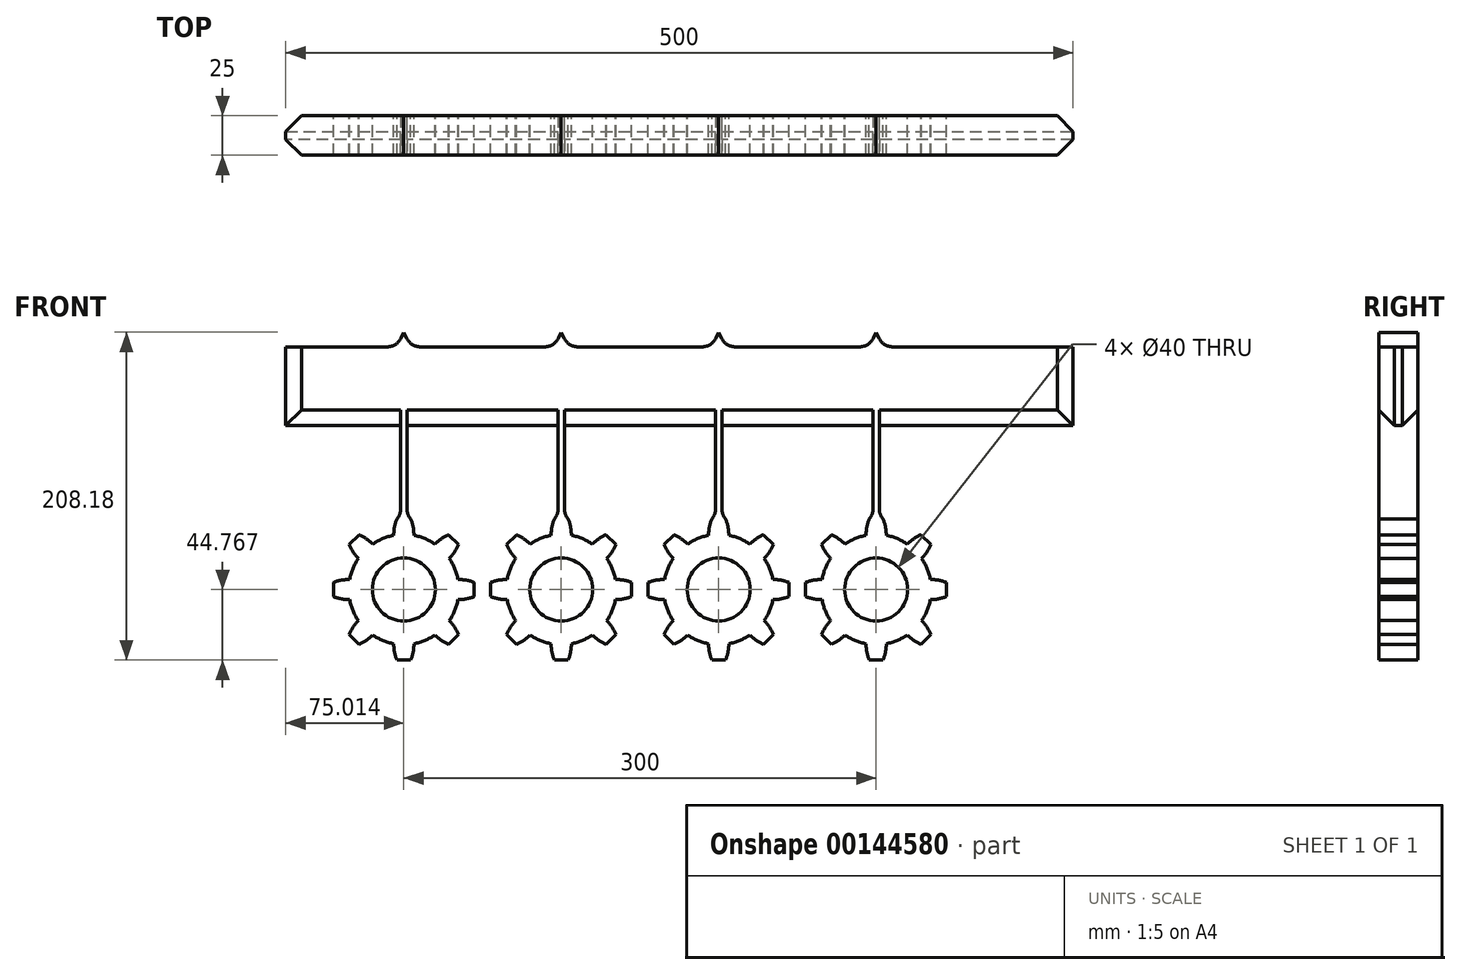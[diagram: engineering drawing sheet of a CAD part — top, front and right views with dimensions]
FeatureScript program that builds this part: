
annotation { "Feature Type Name" : "Feature", "Feature Type Description" : "" }
export const myFeature = defineFeature(function(context is Context, id is Id, definition is map)
    precondition{}
    {
        {
            var Q0;
            Q0=qCreatedBy(makeId("Front.planeOp"),FACE);
            var sketch = newSketch(context, id + "F0", { "sketchPlane" : qUnion([Q0])});
            skLineSegment(sketch, "E0.bottom", {"start": v(-250, 25) * mm, "end": v(-179.31, 25) * mm});
            skLineSegment(sketch, "E0.top", {"start": v(-250, -25) * mm, "end": v(-176.99, -25) * mm});
            skLineSegment(sketch, "E0.left", {"start": v(-250, 25) * mm, "end": v(-250, -25) * mm});
            skLineSegment(sketch, "E0.right", {"start": v(250, 25) * mm, "end": v(250, -25) * mm});
            skLineSegment(sketch, "E1", {"start": v(-174.99, 34.28) * mm, "end": v(-179.31, 25) * mm});
            skLineSegment(sketch, "E2", {"start": v(-174.99, 34.28) * mm, "end": v(-170.66, 25) * mm});
            skLineSegment(sketch, "E3.1.0.0", {"start": v(-74.99, 34.28) * mm, "end": v(-79.31, 25) * mm});
            skLineSegment(sketch, "E3.1.0.1", {"start": v(-74.99, 34.28) * mm, "end": v(-70.66, 25) * mm});
            skLineSegment(sketch, "E3.2.0.0", {"start": v(25.01, 34.28) * mm, "end": v(20.69, 25) * mm});
            skLineSegment(sketch, "E3.2.0.1", {"start": v(25.01, 34.28) * mm, "end": v(29.34, 25) * mm});
            skLineSegment(sketch, "E3.3.0.0", {"start": v(125.01, 34.28) * mm, "end": v(120.69, 25) * mm});
            skLineSegment(sketch, "E3.3.0.1", {"start": v(125.01, 34.28) * mm, "end": v(129.34, 25) * mm});
            skLineSegment(sketch, "E3.direction1", {"start": v(-170.66, 25) * mm, "end": v(-79.31, 25) * mm, "construction": true});
            skLineSegment(sketch, "E4.trimOffspring", {"start": v(-70.66, 25) * mm, "end": v(20.69, 25) * mm});
            skLineSegment(sketch, "E5.trimOffspring", {"start": v(-170.66, 25) * mm, "end": v(-79.31, 25) * mm});
            skLineSegment(sketch, "E6.trimOffspring", {"start": v(29.34, 25) * mm, "end": v(120.69, 25) * mm});
            skLineSegment(sketch, "E7.trimOffspring", {"start": v(129.34, 25) * mm, "end": v(250, 25) * mm});
            skCircle(sketch, "E8", {"center": v(-174.99, -129.13) * mm, "radius": 20 * mm});
            skArc(sketch, "E9", {"start": v(-179.41, -84.37) * mm, "mid": v(-180.9, -89.45) * mm, "end": v(-181.41, -94.73) * mm});
            skLineSegment(sketch, "E10", {"start": v(-179.41, -84.37) * mm, "end": v(-176.99, -84.37) * mm});
            skArc(sketch, "E11", {"start": v(-168.56, -94.73) * mm, "mid": v(-169.06, -89.45) * mm, "end": v(-170.56, -84.37) * mm});
            skArc(sketch, "E12.2.0", {"start": v(16.64, 197.56) * mm, "mid": v(12.99, 201.4) * mm, "end": v(8.67, 204.47) * mm});
            skLineSegment(sketch, "E12.2.1", {"start": v(16.64, 197.56) * mm, "end": v(12.21, 189.9) * mm});
            skArc(sketch, "E12.2.2", {"start": v(2.24, 193.34) * mm, "mid": v(7.06, 191.14) * mm, "end": v(12.21, 189.9) * mm});
            skPoint(sketch, "E12.center", {"position": v(0, 0) * mm});
            skArc(sketch, "E13.1.0", {"start": v(-209.77, -100.61) * mm, "mid": v(-207.23, -105.26) * mm, "end": v(-203.86, -109.35) * mm});
            skLineSegment(sketch, "E13.1.1", {"start": v(-209.77, -100.61) * mm, "end": v(-203.5, -94.35) * mm});
            skArc(sketch, "E13.1.2", {"start": v(-194.77, -100.26) * mm, "mid": v(-198.86, -96.89) * mm, "end": v(-203.5, -94.35) * mm});
            skArc(sketch, "E13.2.0", {"start": v(-219.75, -133.56) * mm, "mid": v(-214.67, -135.05) * mm, "end": v(-209.4, -135.56) * mm});
            skLineSegment(sketch, "E13.2.1", {"start": v(-219.75, -133.56) * mm, "end": v(-219.75, -124.7) * mm});
            skArc(sketch, "E13.2.2", {"start": v(-209.4, -122.7) * mm, "mid": v(-214.67, -123.21) * mm, "end": v(-219.75, -124.7) * mm});
            skArc(sketch, "E13.3.0", {"start": v(-203.5, -163.92) * mm, "mid": v(-198.86, -161.38) * mm, "end": v(-194.77, -158) * mm});
            skLineSegment(sketch, "E13.3.1", {"start": v(-203.5, -163.92) * mm, "end": v(-209.77, -157.66) * mm});
            skArc(sketch, "E13.3.2", {"start": v(-203.86, -148.92) * mm, "mid": v(-207.23, -153) * mm, "end": v(-209.77, -157.66) * mm});
            skArc(sketch, "E13.4.0", {"start": v(-170.56, -173.9) * mm, "mid": v(-169.06, -168.81) * mm, "end": v(-168.56, -163.54) * mm});
            skLineSegment(sketch, "E13.4.1", {"start": v(-170.56, -173.9) * mm, "end": v(-179.41, -173.9) * mm});
            skArc(sketch, "E13.4.2", {"start": v(-181.41, -163.54) * mm, "mid": v(-180.9, -168.81) * mm, "end": v(-179.41, -173.9) * mm});
            skArc(sketch, "E13.5.0", {"start": v(-140.2, -157.66) * mm, "mid": v(-142.74, -153) * mm, "end": v(-146.11, -148.92) * mm});
            skLineSegment(sketch, "E13.5.1", {"start": v(-140.2, -157.66) * mm, "end": v(-146.46, -163.92) * mm});
            skArc(sketch, "E13.5.2", {"start": v(-155.2, -158) * mm, "mid": v(-151.12, -161.38) * mm, "end": v(-146.46, -163.92) * mm});
            skArc(sketch, "E13.6.0", {"start": v(-130.22, -124.7) * mm, "mid": v(-135.3, -123.21) * mm, "end": v(-140.58, -122.7) * mm});
            skLineSegment(sketch, "E13.6.1", {"start": v(-130.22, -124.7) * mm, "end": v(-130.22, -133.56) * mm});
            skArc(sketch, "E13.6.2", {"start": v(-140.58, -135.56) * mm, "mid": v(-135.3, -135.05) * mm, "end": v(-130.22, -133.56) * mm});
            skArc(sketch, "E13.7.0", {"start": v(-146.46, -94.35) * mm, "mid": v(-151.12, -96.89) * mm, "end": v(-155.2, -100.26) * mm});
            skLineSegment(sketch, "E13.7.1", {"start": v(-146.46, -94.35) * mm, "end": v(-140.2, -100.61) * mm});
            skArc(sketch, "E13.7.2", {"start": v(-146.11, -109.35) * mm, "mid": v(-142.74, -105.26) * mm, "end": v(-140.2, -100.61) * mm});
            skArc(sketch, "E14.trimOffspring", {"start": v(-203.86, -109.35) * mm, "mid": v(-207.32, -115.74) * mm, "end": v(-209.4, -122.7) * mm});
            skArc(sketch, "E15.trimOffspring", {"start": v(-194.77, -158) * mm, "mid": v(-188.38, -161.47) * mm, "end": v(-181.41, -163.54) * mm});
            skArc(sketch, "E16.trimOffspring", {"start": v(-168.56, -163.54) * mm, "mid": v(-161.6, -161.47) * mm, "end": v(-155.2, -158) * mm});
            skArc(sketch, "E17.trimOffspring", {"start": v(-209.4, -135.56) * mm, "mid": v(-207.32, -142.53) * mm, "end": v(-203.86, -148.92) * mm});
            skArc(sketch, "E18.trimOffspring", {"start": v(-155.2, -100.26) * mm, "mid": v(-161.6, -96.8) * mm, "end": v(-168.56, -94.73) * mm});
            skArc(sketch, "E19.trimOffspring", {"start": v(-140.58, -122.7) * mm, "mid": v(-142.65, -115.74) * mm, "end": v(-146.11, -109.35) * mm});
            skArc(sketch, "E20.trimOffspring", {"start": v(-146.11, -148.92) * mm, "mid": v(-142.65, -142.53) * mm, "end": v(-140.58, -135.56) * mm});
            skLineSegment(sketch, "E21", {"start": v(-174.99, -84.37) * mm, "end": v(-174.99, -25) * mm, "construction": true});
            skLineSegment(sketch, "E22", {"start": v(-176.99, -84.37) * mm, "end": v(-176.99, -25) * mm});
            skLineSegment(sketch, "E23", {"start": v(-172.99, -84.37) * mm, "end": v(-172.99, -25) * mm});
            skLineSegment(sketch, "E24.trimOffspring", {"start": v(-172.99, -25) * mm, "end": v(23.01, -25) * mm});
            skLineSegment(sketch, "E25.trimOffspring", {"start": v(-172.99, -84.37) * mm, "end": v(-170.56, -84.37) * mm});
            skArc(sketch, "E26", {"start": v(-181.41, -94.73) * mm, "mid": v(-188.38, -96.8) * mm, "end": v(-194.77, -100.26) * mm});
            skCircle(sketch, "E27.1.0.0", {"center": v(-74.99, -129.13) * mm, "radius": 20 * mm});
            skPoint(sketch, "E27.1.0.1", {"position": v(-74.99, -129.13) * mm});
            skArc(sketch, "E27.1.0.2", {"start": v(-94.77, -100.26) * mm, "mid": v(-98.86, -96.89) * mm, "end": v(-103.5, -94.35) * mm});
            skArc(sketch, "E27.1.0.3", {"start": v(-94.77, -158) * mm, "mid": v(-88.38, -161.47) * mm, "end": v(-81.41, -163.54) * mm});
            skArc(sketch, "E27.1.0.4", {"start": v(-109.4, -122.7) * mm, "mid": v(-114.67, -123.21) * mm, "end": v(-119.75, -124.7) * mm});
            skArc(sketch, "E27.1.0.5", {"start": v(-70.56, -173.9) * mm, "mid": v(-69.06, -168.81) * mm, "end": v(-68.56, -163.54) * mm});
            skArc(sketch, "E27.1.0.6", {"start": v(-55.2, -100.26) * mm, "mid": v(-61.6, -96.8) * mm, "end": v(-68.56, -94.73) * mm});
            skArc(sketch, "E27.1.0.7", {"start": v(-40.2, -157.66) * mm, "mid": v(-42.74, -153) * mm, "end": v(-46.11, -148.92) * mm});
            skArc(sketch, "E27.1.0.8", {"start": v(-40.58, -122.7) * mm, "mid": v(-42.65, -115.74) * mm, "end": v(-46.11, -109.35) * mm});
            skArc(sketch, "E27.1.0.9", {"start": v(-46.46, -94.35) * mm, "mid": v(-51.12, -96.89) * mm, "end": v(-55.2, -100.26) * mm});
            skArc(sketch, "E27.1.0.10", {"start": v(-119.75, -133.56) * mm, "mid": v(-114.67, -135.05) * mm, "end": v(-109.4, -135.56) * mm});
            skLineSegment(sketch, "E27.1.0.11", {"start": v(-70.56, -173.9) * mm, "end": v(-79.41, -173.9) * mm});
            skArc(sketch, "E27.1.0.12", {"start": v(-68.56, -94.73) * mm, "mid": v(-69.06, -89.45) * mm, "end": v(-70.56, -84.37) * mm});
            skArc(sketch, "E27.1.0.13", {"start": v(-55.2, -158) * mm, "mid": v(-51.12, -161.38) * mm, "end": v(-46.46, -163.92) * mm});
            skLineSegment(sketch, "E27.1.0.14", {"start": v(-46.46, -94.35) * mm, "end": v(-40.2, -100.61) * mm});
            skArc(sketch, "E27.1.0.15", {"start": v(-40.58, -135.56) * mm, "mid": v(-35.3, -135.05) * mm, "end": v(-30.22, -133.56) * mm});
            skLineSegment(sketch, "E27.1.0.16", {"start": v(-109.77, -100.61) * mm, "end": v(-103.5, -94.35) * mm});
            skArc(sketch, "E27.1.0.17", {"start": v(-81.41, -94.73) * mm, "mid": v(-88.38, -96.8) * mm, "end": v(-94.77, -100.26) * mm});
            skLineSegment(sketch, "E27.1.0.18", {"start": v(-30.22, -124.7) * mm, "end": v(-30.22, -133.56) * mm});
            skArc(sketch, "E27.1.0.19", {"start": v(-103.86, -109.35) * mm, "mid": v(-107.32, -115.74) * mm, "end": v(-109.4, -122.7) * mm});
            skArc(sketch, "E27.1.0.20", {"start": v(-68.56, -163.54) * mm, "mid": v(-61.6, -161.47) * mm, "end": v(-55.2, -158) * mm});
            skArc(sketch, "E27.1.0.21", {"start": v(-109.77, -100.61) * mm, "mid": v(-107.23, -105.26) * mm, "end": v(-103.86, -109.35) * mm});
            skArc(sketch, "E27.1.0.22", {"start": v(-81.41, -163.54) * mm, "mid": v(-80.9, -168.81) * mm, "end": v(-79.41, -173.9) * mm});
            skArc(sketch, "E27.1.0.23", {"start": v(-79.41, -84.37) * mm, "mid": v(-80.9, -89.45) * mm, "end": v(-81.41, -94.73) * mm});
            skArc(sketch, "E27.1.0.24", {"start": v(-46.11, -148.92) * mm, "mid": v(-42.65, -142.53) * mm, "end": v(-40.58, -135.56) * mm});
            skLineSegment(sketch, "E27.1.0.25", {"start": v(-40.2, -157.66) * mm, "end": v(-46.46, -163.92) * mm});
            skLineSegment(sketch, "E27.1.0.26", {"start": v(-119.75, -133.56) * mm, "end": v(-119.75, -124.7) * mm});
            skArc(sketch, "E27.1.0.27", {"start": v(-46.11, -109.35) * mm, "mid": v(-42.74, -105.26) * mm, "end": v(-40.2, -100.61) * mm});
            skArc(sketch, "E27.1.0.28", {"start": v(-103.86, -148.92) * mm, "mid": v(-107.23, -153) * mm, "end": v(-109.77, -157.66) * mm});
            skArc(sketch, "E27.1.0.29", {"start": v(-109.4, -135.56) * mm, "mid": v(-107.32, -142.53) * mm, "end": v(-103.86, -148.92) * mm});
            skArc(sketch, "E27.1.0.30", {"start": v(-103.5, -163.92) * mm, "mid": v(-98.86, -161.38) * mm, "end": v(-94.77, -158) * mm});
            skArc(sketch, "E27.1.0.31", {"start": v(-30.22, -124.7) * mm, "mid": v(-35.3, -123.21) * mm, "end": v(-40.58, -122.7) * mm});
            skLineSegment(sketch, "E27.1.0.32", {"start": v(-103.5, -163.92) * mm, "end": v(-109.77, -157.66) * mm});
            skLineSegment(sketch, "E27.1.0.33", {"start": v(-79.41, -84.37) * mm, "end": v(-76.99, -84.37) * mm});
            skLineSegment(sketch, "E27.1.0.34", {"start": v(-72.99, -84.37) * mm, "end": v(-70.56, -84.37) * mm});
            skLineSegment(sketch, "E27.1.0.35", {"start": v(-76.99, -84.37) * mm, "end": v(-76.99, -25) * mm});
            skLineSegment(sketch, "E27.1.0.36", {"start": v(-72.99, -84.37) * mm, "end": v(-72.99, -25) * mm});
            skCircle(sketch, "E27.2.0.0", {"center": v(25.01, -129.13) * mm, "radius": 20 * mm});
            skPoint(sketch, "E27.2.0.1", {"position": v(25.01, -129.13) * mm});
            skArc(sketch, "E27.2.0.2", {"start": v(5.23, -100.26) * mm, "mid": v(1.14, -96.89) * mm, "end": v(-3.5, -94.35) * mm});
            skArc(sketch, "E27.2.0.3", {"start": v(5.23, -158) * mm, "mid": v(11.62, -161.47) * mm, "end": v(18.59, -163.54) * mm});
            skArc(sketch, "E27.2.0.4", {"start": v(-9.4, -122.7) * mm, "mid": v(-14.67, -123.21) * mm, "end": v(-19.75, -124.7) * mm});
            skArc(sketch, "E27.2.0.5", {"start": v(29.44, -173.9) * mm, "mid": v(30.94, -168.81) * mm, "end": v(31.44, -163.54) * mm});
            skArc(sketch, "E27.2.0.6", {"start": v(44.8, -100.26) * mm, "mid": v(38.4, -96.8) * mm, "end": v(31.44, -94.73) * mm});
            skArc(sketch, "E27.2.0.7", {"start": v(59.8, -157.66) * mm, "mid": v(57.26, -153) * mm, "end": v(53.89, -148.92) * mm});
            skArc(sketch, "E27.2.0.8", {"start": v(59.42, -122.7) * mm, "mid": v(57.35, -115.74) * mm, "end": v(53.89, -109.35) * mm});
            skArc(sketch, "E27.2.0.9", {"start": v(53.54, -94.35) * mm, "mid": v(48.88, -96.89) * mm, "end": v(44.8, -100.26) * mm});
            skArc(sketch, "E27.2.0.10", {"start": v(-19.75, -133.56) * mm, "mid": v(-14.67, -135.05) * mm, "end": v(-9.4, -135.56) * mm});
            skLineSegment(sketch, "E27.2.0.11", {"start": v(29.44, -173.9) * mm, "end": v(20.59, -173.9) * mm});
            skArc(sketch, "E27.2.0.12", {"start": v(31.44, -94.73) * mm, "mid": v(30.94, -89.45) * mm, "end": v(29.44, -84.37) * mm});
            skArc(sketch, "E27.2.0.13", {"start": v(44.8, -158) * mm, "mid": v(48.88, -161.38) * mm, "end": v(53.54, -163.92) * mm});
            skLineSegment(sketch, "E27.2.0.14", {"start": v(53.54, -94.35) * mm, "end": v(59.8, -100.61) * mm});
            skArc(sketch, "E27.2.0.15", {"start": v(59.42, -135.56) * mm, "mid": v(64.7, -135.05) * mm, "end": v(69.78, -133.56) * mm});
            skLineSegment(sketch, "E27.2.0.16", {"start": v(-9.77, -100.61) * mm, "end": v(-3.5, -94.35) * mm});
            skArc(sketch, "E27.2.0.17", {"start": v(18.59, -94.73) * mm, "mid": v(11.62, -96.8) * mm, "end": v(5.23, -100.26) * mm});
            skLineSegment(sketch, "E27.2.0.18", {"start": v(69.78, -124.7) * mm, "end": v(69.78, -133.56) * mm});
            skArc(sketch, "E27.2.0.19", {"start": v(-3.86, -109.35) * mm, "mid": v(-7.32, -115.74) * mm, "end": v(-9.4, -122.7) * mm});
            skArc(sketch, "E27.2.0.20", {"start": v(31.44, -163.54) * mm, "mid": v(38.4, -161.47) * mm, "end": v(44.8, -158) * mm});
            skArc(sketch, "E27.2.0.21", {"start": v(-9.77, -100.61) * mm, "mid": v(-7.23, -105.26) * mm, "end": v(-3.86, -109.35) * mm});
            skArc(sketch, "E27.2.0.22", {"start": v(18.59, -163.54) * mm, "mid": v(19.1, -168.81) * mm, "end": v(20.59, -173.9) * mm});
            skArc(sketch, "E27.2.0.23", {"start": v(20.59, -84.37) * mm, "mid": v(19.1, -89.45) * mm, "end": v(18.59, -94.73) * mm});
            skArc(sketch, "E27.2.0.24", {"start": v(53.89, -148.92) * mm, "mid": v(57.35, -142.53) * mm, "end": v(59.42, -135.56) * mm});
            skLineSegment(sketch, "E27.2.0.25", {"start": v(59.8, -157.66) * mm, "end": v(53.54, -163.92) * mm});
            skLineSegment(sketch, "E27.2.0.26", {"start": v(-19.75, -133.56) * mm, "end": v(-19.75, -124.7) * mm});
            skArc(sketch, "E27.2.0.27", {"start": v(53.89, -109.35) * mm, "mid": v(57.26, -105.26) * mm, "end": v(59.8, -100.61) * mm});
            skArc(sketch, "E27.2.0.28", {"start": v(-3.86, -148.92) * mm, "mid": v(-7.23, -153) * mm, "end": v(-9.77, -157.66) * mm});
            skArc(sketch, "E27.2.0.29", {"start": v(-9.4, -135.56) * mm, "mid": v(-7.32, -142.53) * mm, "end": v(-3.86, -148.92) * mm});
            skArc(sketch, "E27.2.0.30", {"start": v(-3.5, -163.92) * mm, "mid": v(1.14, -161.38) * mm, "end": v(5.23, -158) * mm});
            skArc(sketch, "E27.2.0.31", {"start": v(69.78, -124.7) * mm, "mid": v(64.7, -123.21) * mm, "end": v(59.42, -122.7) * mm});
            skLineSegment(sketch, "E27.2.0.32", {"start": v(-3.5, -163.92) * mm, "end": v(-9.77, -157.66) * mm});
            skLineSegment(sketch, "E27.2.0.33", {"start": v(20.59, -84.37) * mm, "end": v(23.01, -84.37) * mm});
            skLineSegment(sketch, "E27.2.0.34", {"start": v(27.01, -84.37) * mm, "end": v(29.44, -84.37) * mm});
            skLineSegment(sketch, "E27.2.0.35", {"start": v(23.01, -84.37) * mm, "end": v(23.01, -25) * mm});
            skLineSegment(sketch, "E27.2.0.36", {"start": v(27.01, -84.37) * mm, "end": v(27.01, -25) * mm});
            skCircle(sketch, "E27.3.0.0", {"center": v(125.01, -129.13) * mm, "radius": 20 * mm});
            skPoint(sketch, "E27.3.0.1", {"position": v(125.01, -129.13) * mm});
            skArc(sketch, "E27.3.0.2", {"start": v(105.23, -100.26) * mm, "mid": v(101.14, -96.89) * mm, "end": v(96.5, -94.35) * mm});
            skArc(sketch, "E27.3.0.3", {"start": v(105.23, -158) * mm, "mid": v(111.62, -161.47) * mm, "end": v(118.59, -163.54) * mm});
            skArc(sketch, "E27.3.0.4", {"start": v(90.6, -122.7) * mm, "mid": v(85.33, -123.21) * mm, "end": v(80.25, -124.7) * mm});
            skArc(sketch, "E27.3.0.5", {"start": v(129.44, -173.9) * mm, "mid": v(130.94, -168.81) * mm, "end": v(131.44, -163.54) * mm});
            skArc(sketch, "E27.3.0.6", {"start": v(144.8, -100.26) * mm, "mid": v(138.4, -96.8) * mm, "end": v(131.44, -94.73) * mm});
            skArc(sketch, "E27.3.0.7", {"start": v(159.8, -157.66) * mm, "mid": v(157.26, -153) * mm, "end": v(153.89, -148.92) * mm});
            skArc(sketch, "E27.3.0.8", {"start": v(159.42, -122.7) * mm, "mid": v(157.35, -115.74) * mm, "end": v(153.89, -109.35) * mm});
            skArc(sketch, "E27.3.0.9", {"start": v(153.54, -94.35) * mm, "mid": v(148.88, -96.89) * mm, "end": v(144.8, -100.26) * mm});
            skArc(sketch, "E27.3.0.10", {"start": v(80.25, -133.56) * mm, "mid": v(85.33, -135.05) * mm, "end": v(90.6, -135.56) * mm});
            skLineSegment(sketch, "E27.3.0.11", {"start": v(129.44, -173.9) * mm, "end": v(120.59, -173.9) * mm});
            skArc(sketch, "E27.3.0.12", {"start": v(131.44, -94.73) * mm, "mid": v(130.94, -89.45) * mm, "end": v(129.44, -84.37) * mm});
            skArc(sketch, "E27.3.0.13", {"start": v(144.8, -158) * mm, "mid": v(148.88, -161.38) * mm, "end": v(153.54, -163.92) * mm});
            skLineSegment(sketch, "E27.3.0.14", {"start": v(153.54, -94.35) * mm, "end": v(159.8, -100.61) * mm});
            skArc(sketch, "E27.3.0.15", {"start": v(159.42, -135.56) * mm, "mid": v(164.7, -135.05) * mm, "end": v(169.78, -133.56) * mm});
            skLineSegment(sketch, "E27.3.0.16", {"start": v(90.23, -100.61) * mm, "end": v(96.5, -94.35) * mm});
            skArc(sketch, "E27.3.0.17", {"start": v(118.59, -94.73) * mm, "mid": v(111.62, -96.8) * mm, "end": v(105.23, -100.26) * mm});
            skLineSegment(sketch, "E27.3.0.18", {"start": v(169.78, -124.7) * mm, "end": v(169.78, -133.56) * mm});
            skArc(sketch, "E27.3.0.19", {"start": v(96.14, -109.35) * mm, "mid": v(92.68, -115.74) * mm, "end": v(90.6, -122.7) * mm});
            skArc(sketch, "E27.3.0.20", {"start": v(131.44, -163.54) * mm, "mid": v(138.4, -161.47) * mm, "end": v(144.8, -158) * mm});
            skArc(sketch, "E27.3.0.21", {"start": v(90.23, -100.61) * mm, "mid": v(92.77, -105.26) * mm, "end": v(96.14, -109.35) * mm});
            skArc(sketch, "E27.3.0.22", {"start": v(118.59, -163.54) * mm, "mid": v(119.1, -168.81) * mm, "end": v(120.59, -173.9) * mm});
            skArc(sketch, "E27.3.0.23", {"start": v(120.59, -84.37) * mm, "mid": v(119.1, -89.45) * mm, "end": v(118.59, -94.73) * mm});
            skArc(sketch, "E27.3.0.24", {"start": v(153.89, -148.92) * mm, "mid": v(157.35, -142.53) * mm, "end": v(159.42, -135.56) * mm});
            skLineSegment(sketch, "E27.3.0.25", {"start": v(159.8, -157.66) * mm, "end": v(153.54, -163.92) * mm});
            skLineSegment(sketch, "E27.3.0.26", {"start": v(80.25, -133.56) * mm, "end": v(80.25, -124.7) * mm});
            skArc(sketch, "E27.3.0.27", {"start": v(153.89, -109.35) * mm, "mid": v(157.26, -105.26) * mm, "end": v(159.8, -100.61) * mm});
            skArc(sketch, "E27.3.0.28", {"start": v(96.14, -148.92) * mm, "mid": v(92.77, -153) * mm, "end": v(90.23, -157.66) * mm});
            skArc(sketch, "E27.3.0.29", {"start": v(90.6, -135.56) * mm, "mid": v(92.68, -142.53) * mm, "end": v(96.14, -148.92) * mm});
            skArc(sketch, "E27.3.0.30", {"start": v(96.5, -163.92) * mm, "mid": v(101.14, -161.38) * mm, "end": v(105.23, -158) * mm});
            skArc(sketch, "E27.3.0.31", {"start": v(169.78, -124.7) * mm, "mid": v(164.7, -123.21) * mm, "end": v(159.42, -122.7) * mm});
            skLineSegment(sketch, "E27.3.0.32", {"start": v(96.5, -163.92) * mm, "end": v(90.23, -157.66) * mm});
            skLineSegment(sketch, "E27.3.0.33", {"start": v(120.59, -84.37) * mm, "end": v(123.01, -84.37) * mm});
            skLineSegment(sketch, "E27.3.0.34", {"start": v(127.01, -84.37) * mm, "end": v(129.44, -84.37) * mm});
            skLineSegment(sketch, "E27.3.0.35", {"start": v(123.01, -84.37) * mm, "end": v(123.01, -25) * mm});
            skLineSegment(sketch, "E27.3.0.36", {"start": v(127.01, -84.37) * mm, "end": v(127.01, -25) * mm});
            skLineSegment(sketch, "E27.direction1", {"start": v(-203.5, -163.92) * mm, "end": v(-103.5, -163.92) * mm, "construction": true});
            skLineSegment(sketch, "E28.trimOffspring", {"start": v(127.01, -25) * mm, "end": v(250, -25) * mm});
            skLineSegment(sketch, "E29.trimOffspring", {"start": v(27.01, -25) * mm, "end": v(123.01, -25) * mm});
            skSolve(sketch);
        }
        {
            var Q0;
            Q0 = qSketchRegion(id + "F0", true);
            extrude(context, id + "F1", {"entities" : qUnion([Q0]), "endBound" : BoundingType.SYMMETRIC, "depth" : 25 * mm});
        }
        {
            var Q0;
            Q0=makeQuery(id+"F1.opExtrude","SWEPT_EDGE",EDGE,{"disambiguationData":[OSD([sQuery(id+"F0.wireOp",EDGE,"E0.bottom"),sQuery(id+"F0.wireOp",EDGE,"E1")])]});
            var Q1;
            Q1=makeQuery(id+"F1.opExtrude","SWEPT_EDGE",EDGE,{"disambiguationData":[OSD([sQuery(id+"F0.wireOp",EDGE,"E10"),sQuery(id+"F0.wireOp",EDGE,"E22")])]});
            var Q2;
            Q2=makeQuery(id+"F1.opExtrude","SWEPT_EDGE",EDGE,{"disambiguationData":[OSD([sQuery(id+"F0.wireOp",EDGE,"E3.1.0.0"),sQuery(id+"F0.wireOp",EDGE,"E5.trimOffspring")])]});
            var Q3;
            Q3=makeQuery(id+"F1.opExtrude","SWEPT_EDGE",EDGE,{"disambiguationData":[OSD([sQuery(id+"F0.wireOp",EDGE,"E3.2.0.0"),sQuery(id+"F0.wireOp",EDGE,"E4.trimOffspring")])]});
            var Q4;
            Q4=makeQuery(id+"F1.opExtrude","SWEPT_EDGE",EDGE,{"disambiguationData":[OSD([sQuery(id+"F0.wireOp",EDGE,"E3.3.0.0"),sQuery(id+"F0.wireOp",EDGE,"E6.trimOffspring")])]});
            var Q5;
            Q5=makeQuery(id+"F1.opExtrude","SWEPT_EDGE",EDGE,{"disambiguationData":[OSD([sQuery(id+"F0.wireOp",EDGE,"E27.3.0.33"),sQuery(id+"F0.wireOp",EDGE,"E27.3.0.35")])]});
            var Q6;
            Q6=makeQuery(id+"F1.opExtrude","SWEPT_EDGE",EDGE,{"disambiguationData":[OSD([sQuery(id+"F0.wireOp",EDGE,"E27.2.0.33"),sQuery(id+"F0.wireOp",EDGE,"E27.2.0.35")])]});
            var Q7;
            Q7=makeQuery(id+"F1.opExtrude","SWEPT_EDGE",EDGE,{"disambiguationData":[OSD([sQuery(id+"F0.wireOp",EDGE,"E27.1.0.33"),sQuery(id+"F0.wireOp",EDGE,"E27.1.0.35")])]});
            var Q8;
            Q8=makeQuery(id+"F1.opExtrude","SWEPT_EDGE",EDGE,{"disambiguationData":[OSD([sQuery(id+"F0.wireOp",EDGE,"E2"),sQuery(id+"F0.wireOp",EDGE,"E5.trimOffspring")])]});
            var Q9;
            Q9=makeQuery(id+"F1.opExtrude","SWEPT_EDGE",EDGE,{"disambiguationData":[OSD([sQuery(id+"F0.wireOp",EDGE,"E3.1.0.1"),sQuery(id+"F0.wireOp",EDGE,"E4.trimOffspring")])]});
            var Q10;
            Q10=makeQuery(id+"F1.opExtrude","SWEPT_EDGE",EDGE,{"disambiguationData":[OSD([sQuery(id+"F0.wireOp",EDGE,"E3.2.0.1"),sQuery(id+"F0.wireOp",EDGE,"E6.trimOffspring")])]});
            var Q11;
            Q11=makeQuery(id+"F1.opExtrude","SWEPT_EDGE",EDGE,{"disambiguationData":[OSD([sQuery(id+"F0.wireOp",EDGE,"E3.3.0.1"),sQuery(id+"F0.wireOp",EDGE,"E7.trimOffspring")])]});
            var Q12;
            Q12=makeQuery(id+"F1.opExtrude","SWEPT_EDGE",EDGE,{"disambiguationData":[OSD([sQuery(id+"F0.wireOp",EDGE,"E27.1.0.34"),sQuery(id+"F0.wireOp",EDGE,"E27.1.0.36")])]});
            var Q13;
            Q13=makeQuery(id+"F1.opExtrude","SWEPT_EDGE",EDGE,{"disambiguationData":[OSD([sQuery(id+"F0.wireOp",EDGE,"E23"),sQuery(id+"F0.wireOp",EDGE,"E25.trimOffspring")])]});
            var Q14;
            Q14=makeQuery(id+"F1.opExtrude","SWEPT_EDGE",EDGE,{"disambiguationData":[OSD([sQuery(id+"F0.wireOp",EDGE,"E27.2.0.34"),sQuery(id+"F0.wireOp",EDGE,"E27.2.0.36")])]});
            var Q15;
            Q15=makeQuery(id+"F1.opExtrude","SWEPT_EDGE",EDGE,{"disambiguationData":[OSD([sQuery(id+"F0.wireOp",EDGE,"E27.3.0.34"),sQuery(id+"F0.wireOp",EDGE,"E27.3.0.36")])]});
            fillet(context, id + "F2", {"entities" : qUnion([Q0, Q1, Q2, Q3, Q4, Q5, Q6, Q7, Q8, Q9, Q10, Q11, Q12, Q13, Q14, Q15]), "radius" : 10 * mm, "tangentPropagation" : true, "allowEdgeOverflow" : false});
        }
        {
            var Q0;
            Q0=makeQuery(id+"F1.opExtrude","CAP_EDGE",EDGE,{"disambiguationData":[OSD([sQuery(id+"F0.wireOp",EDGE,"E0.left")])],"isStart":false});
            var Q1;
            Q1=makeQuery(id+"F1.opExtrude","CAP_EDGE",EDGE,{"disambiguationData":[OSD([sQuery(id+"F0.wireOp",EDGE,"E0.top")])],"isStart":false});
            var Q2;
            {var subQ0=sQuery(id+"F0.wireOp",EDGE,"E24.trimOffspring");Q2=makeQuery(id+"F1.opExtrude","CAP_EDGE",EDGE,{"disambiguationData":[OSD([subQ0]),TDD([makeQuery(id+"F0.imprint","IMPRINT",EDGE,{"disambiguationData":[TD([[makeQuery(id+"F0.imprint","INTERSECT",VERTEX,{"derivedFrom":[sQuery(id+"F0.wireOp",EDGE,"E23"),subQ0]}),-1.0]])],"derivedFrom":subQ0})])],"isStart":false});}
            var Q3;
            {var subQ0=sQuery(id+"F0.wireOp",EDGE,"E24.trimOffspring");Q3=makeQuery(id+"F1.opExtrude","CAP_EDGE",EDGE,{"disambiguationData":[OSD([subQ0]),TDD([makeQuery(id+"F0.imprint","IMPRINT",EDGE,{"disambiguationData":[TD([[makeQuery(id+"F0.imprint","INTERSECT",VERTEX,{"derivedFrom":[subQ0,sQuery(id+"F0.wireOp",EDGE,"E27.2.0.35")]}),1.0]])],"derivedFrom":subQ0})])],"isStart":false});}
            var Q4;
            Q4=makeQuery(id+"F1.opExtrude","CAP_EDGE",EDGE,{"disambiguationData":[OSD([sQuery(id+"F0.wireOp",EDGE,"E29.trimOffspring")])],"isStart":false});
            var Q5;
            Q5=makeQuery(id+"F1.opExtrude","CAP_EDGE",EDGE,{"disambiguationData":[OSD([sQuery(id+"F0.wireOp",EDGE,"E28.trimOffspring")])],"isStart":false});
            var Q6;
            Q6=makeQuery(id+"F1.opExtrude","CAP_EDGE",EDGE,{"disambiguationData":[OSD([sQuery(id+"F0.wireOp",EDGE,"E0.right")])],"isStart":true});
            var Q7;
            Q7=makeQuery(id+"F1.opExtrude","CAP_EDGE",EDGE,{"disambiguationData":[OSD([sQuery(id+"F0.wireOp",EDGE,"E0.left")])],"isStart":true});
            var Q8;
            Q8=makeQuery(id+"F1.opExtrude","CAP_EDGE",EDGE,{"disambiguationData":[OSD([sQuery(id+"F0.wireOp",EDGE,"E0.top")])],"isStart":true});
            var Q9;
            {var subQ0=sQuery(id+"F0.wireOp",EDGE,"E24.trimOffspring");Q9=makeQuery(id+"F1.opExtrude","CAP_EDGE",EDGE,{"disambiguationData":[OSD([subQ0]),TDD([makeQuery(id+"F0.imprint","IMPRINT",EDGE,{"disambiguationData":[TD([[makeQuery(id+"F0.imprint","INTERSECT",VERTEX,{"derivedFrom":[sQuery(id+"F0.wireOp",EDGE,"E23"),subQ0]}),-1.0]])],"derivedFrom":subQ0})])],"isStart":true});}
            var Q10;
            Q10=makeQuery(id+"F1.opExtrude","CAP_EDGE",EDGE,{"disambiguationData":[OSD([sQuery(id+"F0.wireOp",EDGE,"E28.trimOffspring")])],"isStart":true});
            var Q11;
            Q11=makeQuery(id+"F1.opExtrude","CAP_EDGE",EDGE,{"disambiguationData":[OSD([sQuery(id+"F0.wireOp",EDGE,"E29.trimOffspring")])],"isStart":true});
            var Q12;
            {var subQ0=sQuery(id+"F0.wireOp",EDGE,"E24.trimOffspring");Q12=makeQuery(id+"F1.opExtrude","CAP_EDGE",EDGE,{"disambiguationData":[OSD([subQ0]),TDD([makeQuery(id+"F0.imprint","IMPRINT",EDGE,{"disambiguationData":[TD([[makeQuery(id+"F0.imprint","INTERSECT",VERTEX,{"derivedFrom":[subQ0,sQuery(id+"F0.wireOp",EDGE,"E27.2.0.35")]}),1.0]])],"derivedFrom":subQ0})])],"isStart":true});}
            var Q13;
            Q13=makeQuery(id+"F1.opExtrude","CAP_EDGE",EDGE,{"disambiguationData":[OSD([sQuery(id+"F0.wireOp",EDGE,"E0.right")])],"isStart":false});
            chamfer(context, id + "F3", {"entities" : qUnion([Q0, Q1, Q2, Q3, Q4, Q5, Q6, Q7, Q8, Q9, Q10, Q11, Q12, Q13]), "width" : 10 * mm, "tangentPropagation" : true});
        }
    });
